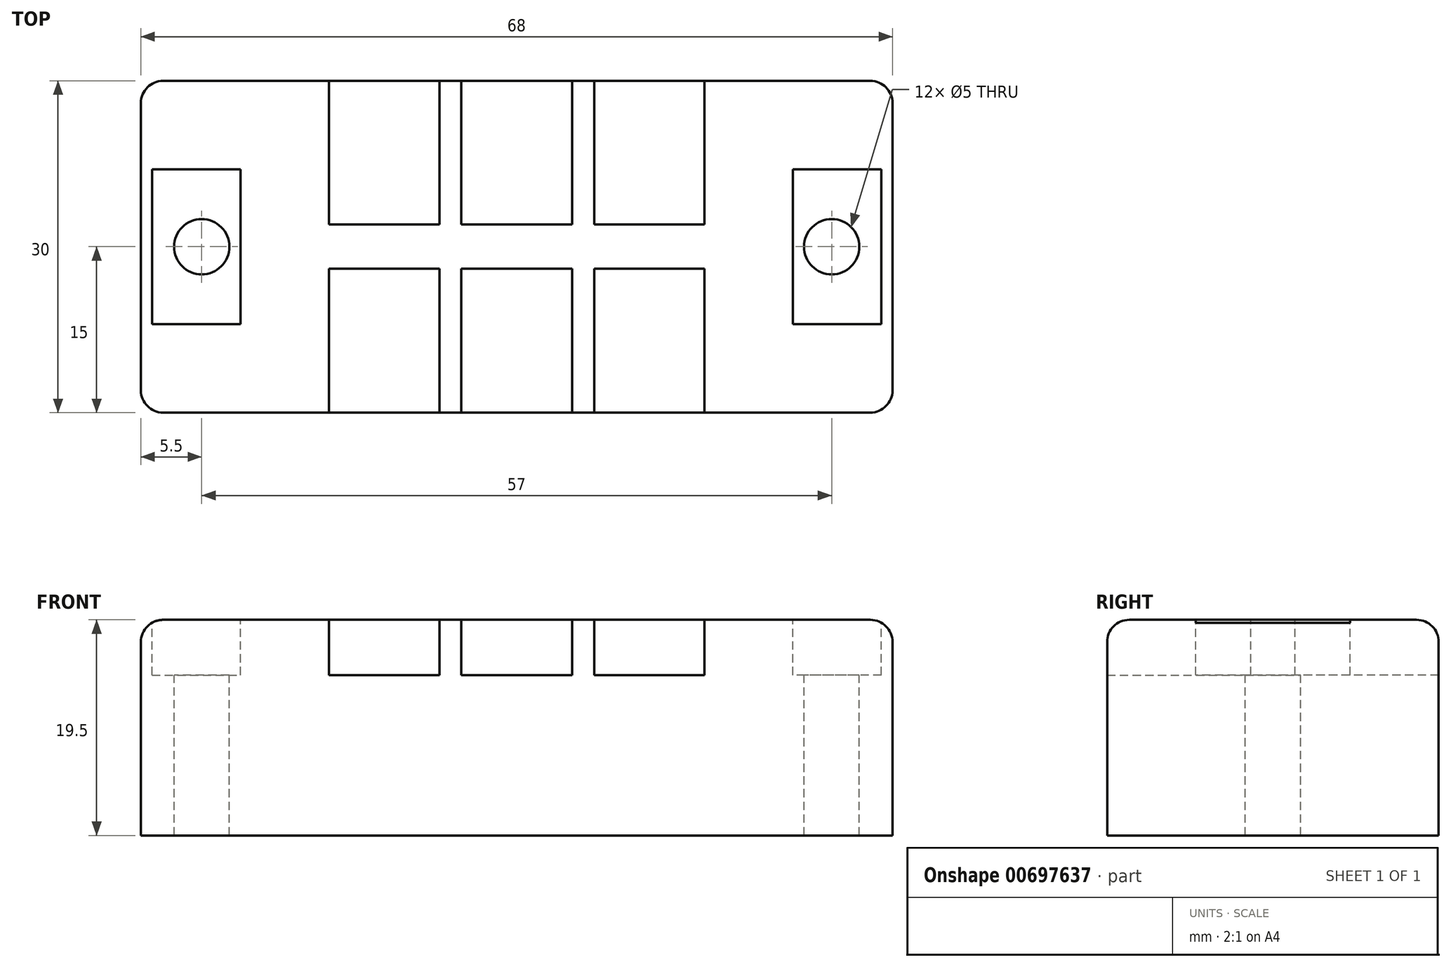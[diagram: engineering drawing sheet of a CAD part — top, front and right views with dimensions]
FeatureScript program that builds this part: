
annotation { "Feature Type Name" : "Feature", "Feature Type Description" : "" }
export const myFeature = defineFeature(function(context is Context, id is Id, definition is map)
    precondition{}
    {
        {
            var Q0;
            Q0=qCreatedBy(makeId("Top.planeOp"),FACE);
            var sketch = newSketch(context, id + "F0", { "sketchPlane" : qUnion([Q0])});
            skLineSegment(sketch, "E0.bottom", {"start": v(34, -15) * mm, "end": v(-34, -15) * mm});
            skLineSegment(sketch, "E0.top", {"start": v(34, 15) * mm, "end": v(-34, 15) * mm});
            skLineSegment(sketch, "E0.left", {"start": v(34, -15) * mm, "end": v(34, 15) * mm});
            skLineSegment(sketch, "E0.right", {"start": v(-34, -15) * mm, "end": v(-34, 15) * mm});
            skPoint(sketch, "E0.middle", {"position": v(0, 0) * mm});
            skSolve(sketch);
        }
        {
            var Q0;
            Q0 = qSketchRegion(id + "F0", true);
            extrude(context, id + "F1", {"entities" : qUnion([Q0]), "depth" : 19.5 * mm, "offsetDistance" : 25 * mm});
        }
        {
            var Q0;
            Q0=makeQuery(id+"F1.opExtrude","CAP_FACE",FACE,{"disambiguationData":[OSD([sQuery(id+"F0.wireOp",EDGE,"E0.bottom"),sQuery(id+"F0.wireOp",EDGE,"E0.top"),sQuery(id+"F0.wireOp",EDGE,"E0.left"),sQuery(id+"F0.wireOp",EDGE,"E0.right")])],"isStart":false});
            var sketch = newSketch(context, id + "F2", { "sketchPlane" : qUnion([Q0])});
            skCircle(sketch, "E1", {"center": v(-28.5, 0) * mm, "radius": 2.5 * mm});
            skCircle(sketch, "E2.MirrorC", {"center": v(28.5, 0) * mm, "radius": 2.5 * mm});
            skSolve(sketch);
        }
        {
            var Q0;
            Q0 = qSketchRegion(id + "F2", true);
            var Q1;
            Q1=makeQuery(id+"F1.opExtrude","CAP_FACE",FACE,{"disambiguationData":[OSD([sQuery(id+"F0.wireOp",EDGE,"E0.bottom"),sQuery(id+"F0.wireOp",EDGE,"E0.top"),sQuery(id+"F0.wireOp",EDGE,"E0.left"),sQuery(id+"F0.wireOp",EDGE,"E0.right")])],"isStart":true});
            extrude(context, id + "F3", {"entities" : qUnion([Q0]), "operationType" : NewBodyOperationType.REMOVE, "endBound" : BoundingType.UP_TO_SURFACE, "oppositeDirection" : true, "depth" : 25 * mm, "endBoundEntityFace" : qUnion([Q1]), "offsetDistance" : 25 * mm});
        }
        {
            var Q0;
            Q0=makeQuery(id+"F1.opExtrude","CAP_FACE",FACE,{"disambiguationData":[OSD([sQuery(id+"F0.wireOp",EDGE,"E0.bottom"),sQuery(id+"F0.wireOp",EDGE,"E0.top"),sQuery(id+"F0.wireOp",EDGE,"E0.left"),sQuery(id+"F0.wireOp",EDGE,"E0.right")])],"isStart":false});
            var sketch = newSketch(context, id + "F4", { "sketchPlane" : qUnion([Q0])});
            skLineSegment(sketch, "E3.bottom", {"start": v(-5, 15) * mm, "end": v(5, 15) * mm});
            skLineSegment(sketch, "E3.top", {"start": v(-5, 2) * mm, "end": v(5, 2) * mm});
            skLineSegment(sketch, "E3.left", {"start": v(-5, 15) * mm, "end": v(-5, 2) * mm});
            skLineSegment(sketch, "E3.right", {"start": v(5, 15) * mm, "end": v(5, 2) * mm});
            skLineSegment(sketch, "E4.bottom", {"start": v(7, 15) * mm, "end": v(17, 15) * mm});
            skLineSegment(sketch, "E4.top", {"start": v(7, 2) * mm, "end": v(17, 2) * mm});
            skLineSegment(sketch, "E4.left", {"start": v(7, 15) * mm, "end": v(7, 2) * mm});
            skLineSegment(sketch, "E4.right", {"start": v(17, 15) * mm, "end": v(17, 2) * mm});
            skLineSegment(sketch, "E5.MirrorCS", {"start": v(-7, 15) * mm, "end": v(-7, 2) * mm});
            skLineSegment(sketch, "E6.MirrorCS", {"start": v(-17, 15) * mm, "end": v(-17, 2) * mm});
            skLineSegment(sketch, "E7.MirrorCS", {"start": v(-7, 2) * mm, "end": v(-17, 2) * mm});
            skLineSegment(sketch, "E8.MirrorCS", {"start": v(-7, 15) * mm, "end": v(-17, 15) * mm});
            skLineSegment(sketch, "E9.MirrorCS", {"start": v(-17, -15) * mm, "end": v(-17, -2) * mm});
            skLineSegment(sketch, "E10.MirrorCS", {"start": v(-7, -2) * mm, "end": v(-17, -2) * mm});
            skLineSegment(sketch, "E11.MirrorCS", {"start": v(-7, -15) * mm, "end": v(-7, -2) * mm});
            skLineSegment(sketch, "E12.MirrorCS", {"start": v(-7, -15) * mm, "end": v(-17, -15) * mm});
            skLineSegment(sketch, "E13.MirrorCS", {"start": v(-5, -15) * mm, "end": v(-5, -2) * mm});
            skLineSegment(sketch, "E14.MirrorCS", {"start": v(-5, -15) * mm, "end": v(5, -15) * mm});
            skLineSegment(sketch, "E15.MirrorCS", {"start": v(5, -15) * mm, "end": v(5, -2) * mm});
            skLineSegment(sketch, "E16.MirrorCS", {"start": v(-5, -2) * mm, "end": v(5, -2) * mm});
            skLineSegment(sketch, "E17.MirrorCS", {"start": v(7, -15) * mm, "end": v(7, -2) * mm});
            skLineSegment(sketch, "E18.MirrorCS", {"start": v(7, -2) * mm, "end": v(17, -2) * mm});
            skLineSegment(sketch, "E19.MirrorCS", {"start": v(17, -15) * mm, "end": v(17, -2) * mm});
            skLineSegment(sketch, "E20.MirrorCS", {"start": v(7, -15) * mm, "end": v(17, -15) * mm});
            skLineSegment(sketch, "E21.bottom", {"start": v(33, 7) * mm, "end": v(25, 7) * mm});
            skLineSegment(sketch, "E21.top", {"start": v(33, -7) * mm, "end": v(25, -7) * mm});
            skLineSegment(sketch, "E21.left", {"start": v(33, 7) * mm, "end": v(33, -7) * mm});
            skLineSegment(sketch, "E21.right", {"start": v(25, 7) * mm, "end": v(25, -7) * mm});
            skLineSegment(sketch, "E22.MirrorCS", {"start": v(-25, 7) * mm, "end": v(-25, -7) * mm});
            skLineSegment(sketch, "E23.MirrorCS", {"start": v(-33, 7) * mm, "end": v(-25, 7) * mm});
            skLineSegment(sketch, "E24.MirrorCS", {"start": v(-33, 7) * mm, "end": v(-33, -7) * mm});
            skLineSegment(sketch, "E25.MirrorCS", {"start": v(-33, -7) * mm, "end": v(-25, -7) * mm});
            skSolve(sketch);
        }
        {
            var Q0;
            Q0 = qSketchRegion(id + "F4", true);
            extrude(context, id + "F5", {"entities" : qUnion([Q0]), "operationType" : NewBodyOperationType.REMOVE, "oppositeDirection" : true, "depth" : 5 * mm, "offsetDistance" : 25 * mm});
        }
        {
            var Q0;
            {var subQ0=sQuery(id+"F0.wireOp",EDGE,"E0.bottom");var subQ1=sQuery(id+"F0.wireOp",EDGE,"E0.right");Q0=makeQuery(id+"F5.boolean.opBoolean","SPLIT",EDGE,{"disambiguationData":[TD([makeQuery(id+"F1.opExtrude","SWEPT_FACE",FACE,{"disambiguationData":[OSD([subQ1])]})])],"derivedFrom":makeQuery(id+"F1.opExtrude","CAP_EDGE",EDGE,{"disambiguationData":[OSD([subQ0])],"isStart":false})});}
            var Q1;
            Q1=makeQuery(id+"F1.opExtrude","CAP_EDGE",EDGE,{"disambiguationData":[OSD([sQuery(id+"F0.wireOp",EDGE,"E0.right")])],"isStart":false});
            var Q2;
            {var subQ0=sQuery(id+"F0.wireOp",EDGE,"E0.right");var subQ1=sQuery(id+"F0.wireOp",EDGE,"E0.top");Q2=makeQuery(id+"F5.boolean.opBoolean","SPLIT",EDGE,{"disambiguationData":[TD([makeQuery(id+"F1.opExtrude","SWEPT_FACE",FACE,{"disambiguationData":[OSD([subQ0])]})])],"derivedFrom":makeQuery(id+"F1.opExtrude","CAP_EDGE",EDGE,{"disambiguationData":[OSD([subQ1])],"isStart":false})});}
            var Q3;
            {var subQ0=sQuery(id+"F0.wireOp",EDGE,"E0.bottom");var subQ1=sQuery(id+"F0.wireOp",EDGE,"E0.left");Q3=makeQuery(id+"F5.boolean.opBoolean","SPLIT",EDGE,{"disambiguationData":[TD([makeQuery(id+"F1.opExtrude","SWEPT_FACE",FACE,{"disambiguationData":[OSD([subQ1])]})])],"derivedFrom":makeQuery(id+"F1.opExtrude","CAP_EDGE",EDGE,{"disambiguationData":[OSD([subQ0])],"isStart":false})});}
            var Q4;
            Q4=makeQuery(id+"F1.opExtrude","CAP_EDGE",EDGE,{"disambiguationData":[OSD([sQuery(id+"F0.wireOp",EDGE,"E0.left")])],"isStart":false});
            var Q5;
            {var subQ0=sQuery(id+"F0.wireOp",EDGE,"E0.left");var subQ1=sQuery(id+"F0.wireOp",EDGE,"E0.top");Q5=makeQuery(id+"F5.boolean.opBoolean","SPLIT",EDGE,{"disambiguationData":[TD([makeQuery(id+"F1.opExtrude","SWEPT_FACE",FACE,{"disambiguationData":[OSD([subQ0])]})])],"derivedFrom":makeQuery(id+"F1.opExtrude","CAP_EDGE",EDGE,{"disambiguationData":[OSD([subQ1])],"isStart":false})});}
            var Q6;
            {var subQ0=sQuery(id+"F0.wireOp",EDGE,"E0.bottom");Q6=makeQuery(id+"F5.boolean.opBoolean","SPLIT",EDGE,{"disambiguationData":[TD([makeQuery(id+"F5.opExtrude","SWEPT_FACE",FACE,{"disambiguationData":[OSD([sQuery(id+"F4.wireOp",EDGE,"E15.MirrorCS")])]})])],"derivedFrom":makeQuery(id+"F1.opExtrude","CAP_EDGE",EDGE,{"disambiguationData":[OSD([subQ0])],"isStart":false})});}
            var Q7;
            {var subQ0=sQuery(id+"F0.wireOp",EDGE,"E0.bottom");Q7=makeQuery(id+"F5.boolean.opBoolean","SPLIT",EDGE,{"disambiguationData":[TD([makeQuery(id+"F5.opExtrude","SWEPT_FACE",FACE,{"disambiguationData":[OSD([sQuery(id+"F4.wireOp",EDGE,"E11.MirrorCS")])]})])],"derivedFrom":makeQuery(id+"F1.opExtrude","CAP_EDGE",EDGE,{"disambiguationData":[OSD([subQ0])],"isStart":false})});}
            var Q8;
            {var subQ0=sQuery(id+"F0.wireOp",EDGE,"E0.top");Q8=makeQuery(id+"F5.boolean.opBoolean","SPLIT",EDGE,{"disambiguationData":[TD([makeQuery(id+"F5.opExtrude","SWEPT_FACE",FACE,{"disambiguationData":[OSD([sQuery(id+"F4.wireOp",EDGE,"E3.right")])]})])],"derivedFrom":makeQuery(id+"F1.opExtrude","CAP_EDGE",EDGE,{"disambiguationData":[OSD([subQ0])],"isStart":false})});}
            var Q9;
            {var subQ0=sQuery(id+"F0.wireOp",EDGE,"E0.top");Q9=makeQuery(id+"F5.boolean.opBoolean","SPLIT",EDGE,{"disambiguationData":[TD([makeQuery(id+"F5.opExtrude","SWEPT_FACE",FACE,{"disambiguationData":[OSD([sQuery(id+"F4.wireOp",EDGE,"E3.left")])]})])],"derivedFrom":makeQuery(id+"F1.opExtrude","CAP_EDGE",EDGE,{"disambiguationData":[OSD([subQ0])],"isStart":false})});}
            var Q10;
            Q10=makeQuery(id+"F1.opExtrude","SWEPT_EDGE",EDGE,{"disambiguationData":[OSD([sQuery(id+"F0.wireOp",EDGE,"E0.bottom"),sQuery(id+"F0.wireOp",EDGE,"E0.right")])]});
            var Q11;
            Q11=makeQuery(id+"F1.opExtrude","SWEPT_EDGE",EDGE,{"disambiguationData":[OSD([sQuery(id+"F0.wireOp",EDGE,"E0.top"),sQuery(id+"F0.wireOp",EDGE,"E0.right")])]});
            var Q12;
            Q12=makeQuery(id+"F1.opExtrude","SWEPT_EDGE",EDGE,{"disambiguationData":[OSD([sQuery(id+"F0.wireOp",EDGE,"E0.top"),sQuery(id+"F0.wireOp",EDGE,"E0.left")])]});
            var Q13;
            Q13=makeQuery(id+"F1.opExtrude","SWEPT_EDGE",EDGE,{"disambiguationData":[OSD([sQuery(id+"F0.wireOp",EDGE,"E0.bottom"),sQuery(id+"F0.wireOp",EDGE,"E0.left")])]});
            fillet(context, id + "F6", {"entities" : qUnion([Q0, Q1, Q2, Q3, Q4, Q5, Q6, Q7, Q8, Q9, Q10, Q11, Q12, Q13]), "radius" : 2 * mm, "tangentPropagation" : true, "allowEdgeOverflow" : false});
        }
    });
